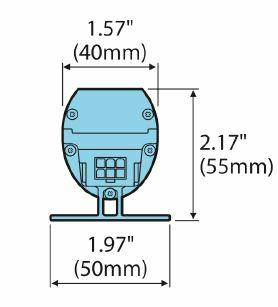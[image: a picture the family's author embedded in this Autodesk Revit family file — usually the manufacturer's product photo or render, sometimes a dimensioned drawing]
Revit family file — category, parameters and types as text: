
# Revit family: Lighting-Linear-Acclaim-XTR DV
name_source: partatom
category: Lighting Fixtures
units: mm (PartAtom-declared; Revit-internal decimal feet)

## family parameters
Cut with Voids When Loaded = No
Host = Face
Light Source = Yes
Part Type = Normal
Room Calculation Point = No
Round Connector Dimension = Use Diameter
Shared = No

## types (1)
- Lighting-Linear-Acclaim-XTR DV
    Apparent Load = 0 VA
    Color Filter = 16777215
    Default Elevation = 48 "
    Description = Linear LED
    Dimming Lamp Color Temperature Shift = <None>
    Emit from Line Length = 48 "
    Height = 2.78 "
    Housing Finish = Aluminum
    Lamp = LED
    Length = 48 "
    Manufacturer = Acclaim Lighting
    Model = Linear XTR DV
    Number of Poles = 1
    Photometric Web File = Load File
    Power Factor = 1
    Tilt Angle = -90.00°
    URL = http://www.acclaimlighting.com
    Voltage = 0 V
    Width = 1.73 "

## geometry (parser evidence)
native form markers: Blend x13, Sweep x2
no freeform markers — native parametric forms only
